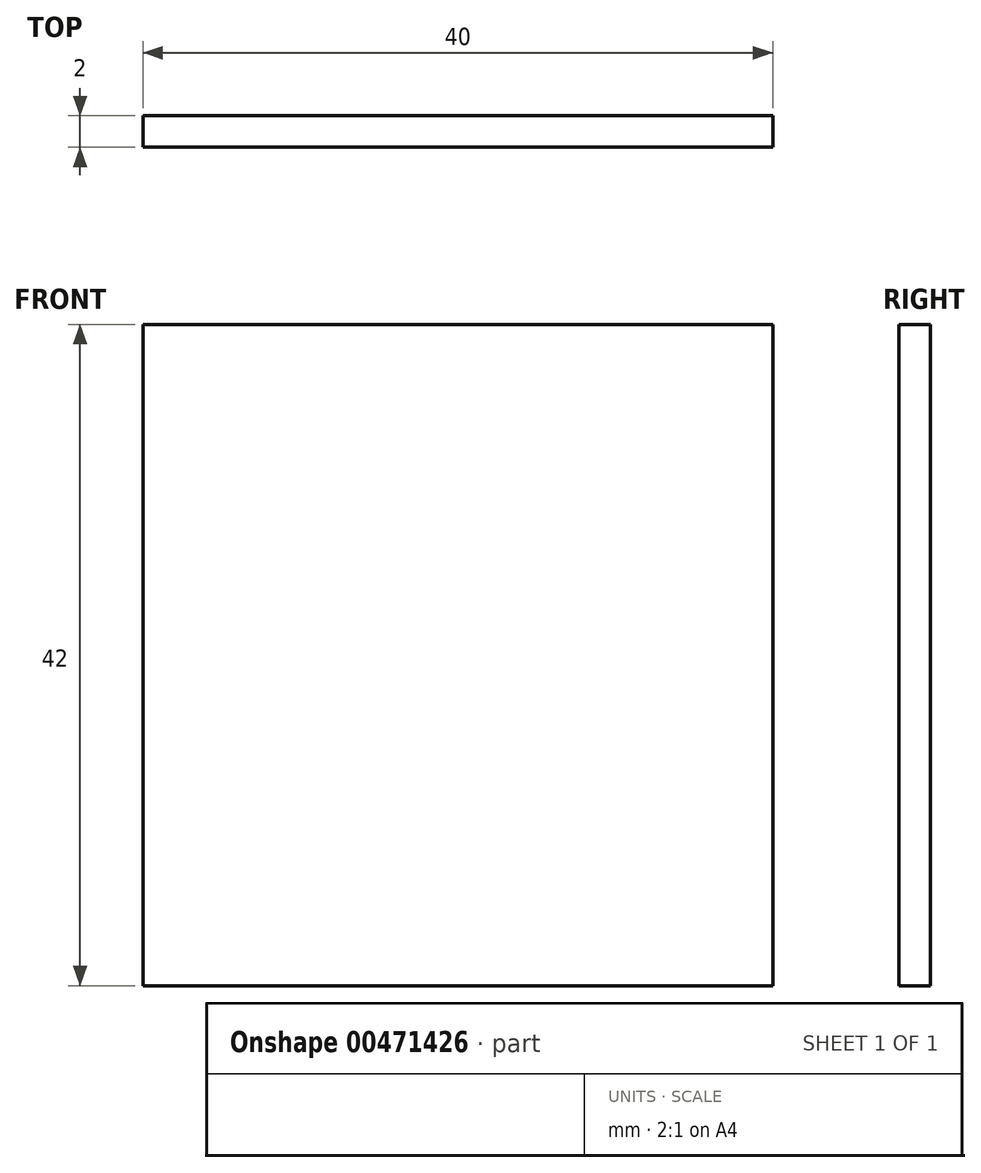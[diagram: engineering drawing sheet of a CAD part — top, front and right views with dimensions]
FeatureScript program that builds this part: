
annotation { "Feature Type Name" : "Feature", "Feature Type Description" : "" }
export const myFeature = defineFeature(function(context is Context, id is Id, definition is map)
    precondition{}
    {
        {
            var Q0;
            Q0=qCreatedBy(makeId("Front.planeOp"),FACE);
            var sketch = newSketch(context, id + "F0", { "sketchPlane" : qUnion([Q0])});
            skLineSegment(sketch, "E0.bottom", {"start": v(0, 0) * mm, "end": v(40, 0) * mm});
            skLineSegment(sketch, "E0.top", {"start": v(0, 42) * mm, "end": v(40, 42) * mm});
            skLineSegment(sketch, "E0.left", {"start": v(0, 0) * mm, "end": v(0, 42) * mm});
            skLineSegment(sketch, "E0.right", {"start": v(40, 0) * mm, "end": v(40, 42) * mm});
            skSolve(sketch);
        }
        {
            var Q0;
            Q0 = qSketchRegion(id + "F0", true);
            extrude(context, id + "F1", {"entities" : qUnion([Q0]), "depth" : 2 * mm});
        }
    });
